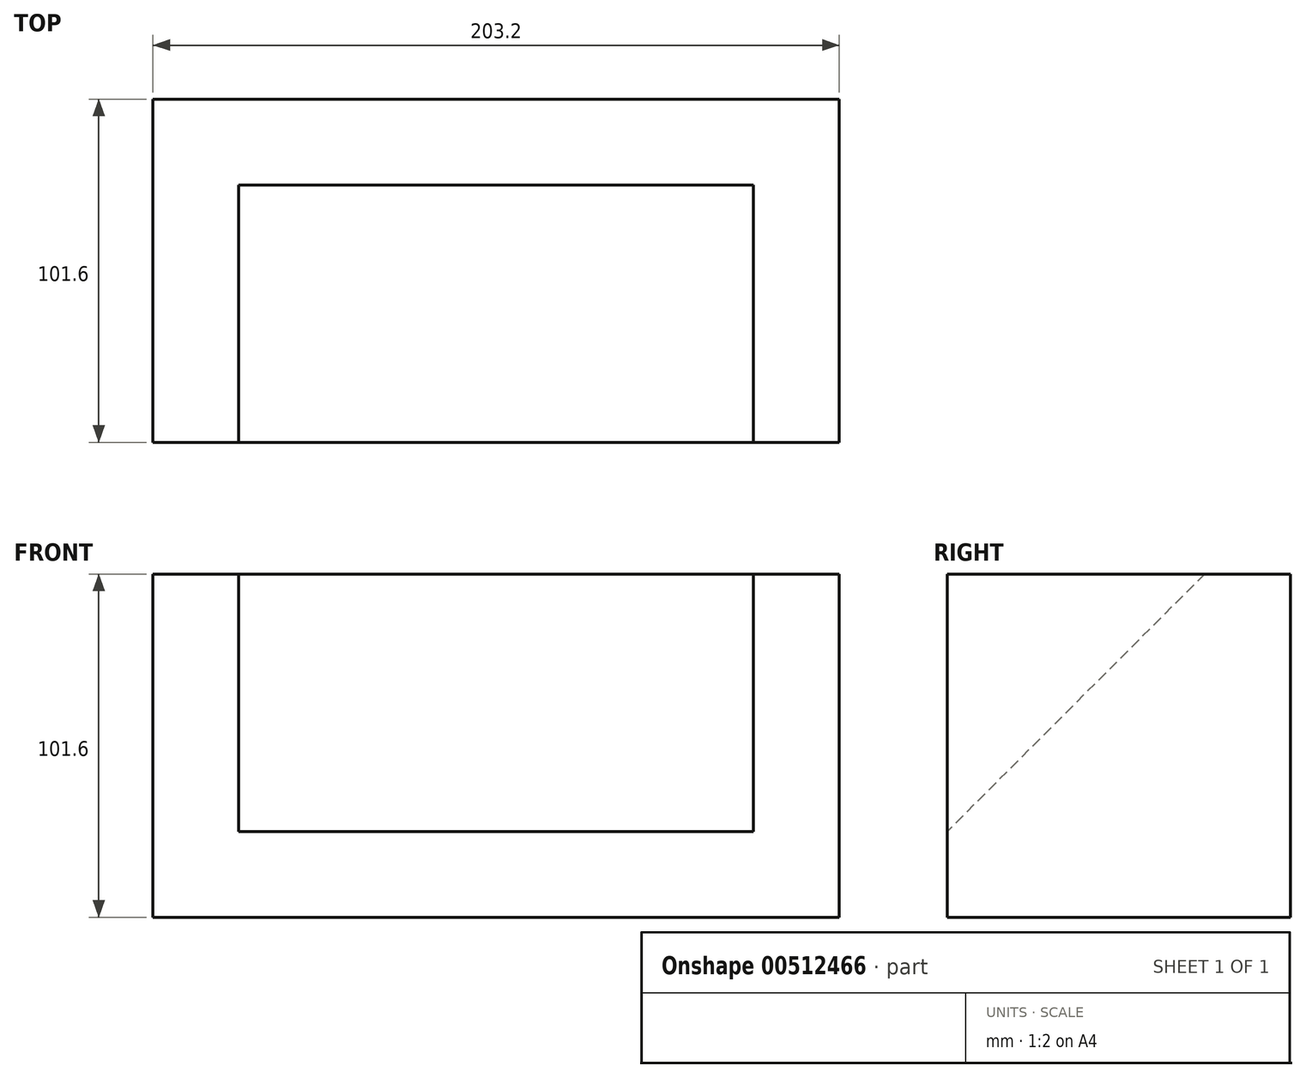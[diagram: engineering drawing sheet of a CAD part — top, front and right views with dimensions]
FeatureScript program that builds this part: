
annotation { "Feature Type Name" : "Feature", "Feature Type Description" : "" }
export const myFeature = defineFeature(function(context is Context, id is Id, definition is map)
    precondition{}
    {
        {
            var Q0;
            Q0=qCreatedBy(makeId("Front.planeOp"),FACE);
            var sketch = newSketch(context, id + "F0", { "sketchPlane" : qUnion([Q0])});
            skLineSegment(sketch, "E0.bottom", {"start": v(0, 0) * mm, "end": v(152.4, 0) * mm});
            skLineSegment(sketch, "E0.top", {"start": v(0, 101.6) * mm, "end": v(152.4, 101.6) * mm});
            skLineSegment(sketch, "E0.left", {"start": v(0, 0) * mm, "end": v(0, 101.6) * mm});
            skLineSegment(sketch, "E0.right", {"start": v(152.4, 0) * mm, "end": v(152.4, 101.6) * mm});
            skSolve(sketch);
        }
        {
            var Q0;
            Q0 = qSketchRegion(id + "F0", true);
            extrude(context, id + "F1", {"entities" : qUnion([Q0]), "depth" : 101.6 * mm});
        }
        {
            var Q0;
            Q0=makeQuery(id+"F1.opExtrude","CAP_EDGE",EDGE,{"disambiguationData":[OSD([sQuery(id+"F0.wireOp",EDGE,"E0.top")])],"isStart":false});
            chamfer(context, id + "F2", {"entities" : qUnion([Q0]), "width" : 76.2 * mm, "tangentPropagation" : true});
        }
        {
            var Q0;
            Q0=makeQuery(id+"F1.opExtrude","SWEPT_FACE",FACE,{"disambiguationData":[OSD([sQuery(id+"F0.wireOp",EDGE,"E0.right")])]});
            var sketch = newSketch(context, id + "F3", { "sketchPlane" : qUnion([Q0])});
            skLineSegment(sketch, "E1.bottom", {"start": v(0, 0) * mm, "end": v(-101.6, 0) * mm});
            skLineSegment(sketch, "E1.top", {"start": v(0, 25.4) * mm, "end": v(-101.6, 25.4) * mm});
            skLineSegment(sketch, "E1.left", {"start": v(0, 0) * mm, "end": v(0, 25.4) * mm});
            skLineSegment(sketch, "E1.right", {"start": v(-101.6, 0) * mm, "end": v(-101.6, 25.4) * mm});
            skSolve(sketch);
        }
        {
            var Q0;
            Q0 = qSketchRegion(id + "F3", true);
            extrude(context, id + "F4", {"entities" : qUnion([Q0]), "operationType" : NewBodyOperationType.ADD, "depth" : 25.4 * mm});
        }
        {
            var Q0;
            Q0=makeQuery(id+"F4.opExtrude","SWEPT_FACE",FACE,{"disambiguationData":[OSD([sQuery(id+"F3.wireOp",EDGE,"E1.top")])]});
            var sketch = newSketch(context, id + "F5", { "sketchPlane" : qUnion([Q0])});
            skLineSegment(sketch, "E2.bottom", {"start": v(177.8, -101.6) * mm, "end": v(152.4, -101.6) * mm});
            skLineSegment(sketch, "E2.top", {"start": v(177.8, 0) * mm, "end": v(152.4, 0) * mm});
            skLineSegment(sketch, "E2.left", {"start": v(177.8, -101.6) * mm, "end": v(177.8, 0) * mm});
            skLineSegment(sketch, "E2.right", {"start": v(152.4, -101.6) * mm, "end": v(152.4, 0) * mm});
            skSolve(sketch);
        }
        {
            var Q0;
            Q0 = qSketchRegion(id + "F5", true);
            extrude(context, id + "F6", {"entities" : qUnion([Q0]), "operationType" : NewBodyOperationType.ADD, "depth" : 76.2 * mm});
        }
        {
            var Q0;
            Q0=makeQuery(id+"F1.opExtrude","SWEPT_FACE",FACE,{"disambiguationData":[OSD([sQuery(id+"F0.wireOp",EDGE,"E0.left")])]});
            var sketch = newSketch(context, id + "F7", { "sketchPlane" : qUnion([Q0])});
            skLineSegment(sketch, "E3.bottom", {"start": v(0, 0) * mm, "end": v(101.6, 0) * mm});
            skLineSegment(sketch, "E3.top", {"start": v(0, 25.4) * mm, "end": v(101.6, 25.4) * mm});
            skLineSegment(sketch, "E3.left", {"start": v(0, 0) * mm, "end": v(0, 25.4) * mm});
            skLineSegment(sketch, "E3.right", {"start": v(101.6, 0) * mm, "end": v(101.6, 25.4) * mm});
            skSolve(sketch);
        }
        {
            var Q0;
            Q0=makeQuery(id+"F7.imprint","IMPRINT",FACE,{"disambiguationData":[TD([[makeQuery(id+"F7.imprint","IMPRINT",EDGE,{"derivedFrom":sQuery(id+"F7.wireOp",EDGE,"E3.bottom")}),-1.0]])]});
            extrude(context, id + "F8", {"entities" : qUnion([Q0]), "operationType" : NewBodyOperationType.ADD, "depth" : 25.4 * mm});
        }
        {
            var Q0;
            Q0=makeQuery(id+"F8.opExtrude","SWEPT_FACE",FACE,{"disambiguationData":[OSD([sQuery(id+"F7.wireOp",EDGE,"E3.top")])]});
            var sketch = newSketch(context, id + "F9", { "sketchPlane" : qUnion([Q0])});
            skLineSegment(sketch, "E4.bottom", {"start": v(0, 0) * mm, "end": v(-25.4, 0) * mm});
            skLineSegment(sketch, "E4.top", {"start": v(0, -101.6) * mm, "end": v(-25.4, -101.6) * mm});
            skLineSegment(sketch, "E4.left", {"start": v(0, 0) * mm, "end": v(0, -101.6) * mm});
            skLineSegment(sketch, "E4.right", {"start": v(-25.4, 0) * mm, "end": v(-25.4, -101.6) * mm});
            skSolve(sketch);
        }
        {
            var Q0;
            Q0=makeQuery(id+"F9.imprint","IMPRINT",FACE,{"disambiguationData":[TD([[makeQuery(id+"F9.imprint","IMPRINT",EDGE,{"derivedFrom":sQuery(id+"F9.wireOp",EDGE,"E4.bottom")}),-1.0]])]});
            extrude(context, id + "F10", {"entities" : qUnion([Q0]), "operationType" : NewBodyOperationType.ADD, "depth" : 76.2 * mm});
        }
    });
